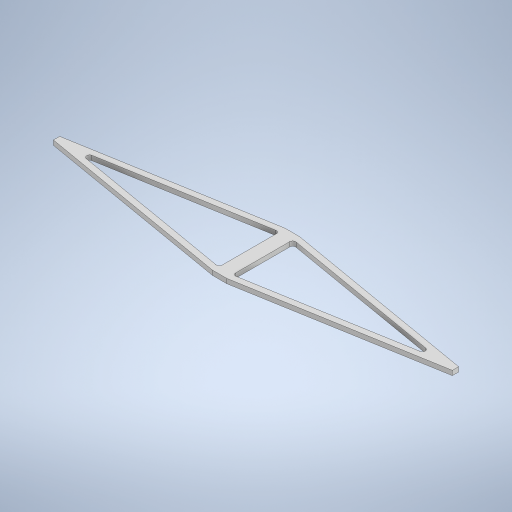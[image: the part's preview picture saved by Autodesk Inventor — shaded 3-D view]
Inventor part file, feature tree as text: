
AUTODESK INVENTOR PART (.ipt)
format: ipt  version: 2023 (Build 270158000, 158)  size: 299,008 bytes
history: native  units: mm
features: extrude x2, sketch x2, fillet x1
ambient origin geometry x8: Origin, YZ Plane, XZ Plane, XY Plane, X Axis, Y Axis, Z Axis, Center Point
bodies: Solid1 (feature_tree)
feature tree (5):
  extrude  "Main_block"  Depth=6.35mm TaperAngle=0.0deg
  fillet  "Fillet7"  Radius=600.0mm
  extrude  "Extrusion4"  Depth=100.0mm
  sketch  "Sketch1"  dims[d6=100.0mm d8=6.35mm d9=0.0mm d36=600.0mm]
  sketch  "Sketch4"  dims[d38=10.0mm d39=100.0mm d44=8.0mm d45=8.0mm d46=4.0mm d47=600.0mm d49=300.0mm d51=0.0mm d52=300.0mm d53=300.0mm d54=0.0mm d55=0.0mm d56=0.0mm d57=0.0mm d60=0.0mm d62=10.0mm d63=0.0mm d37=0.0mm d48=0.0mm]
